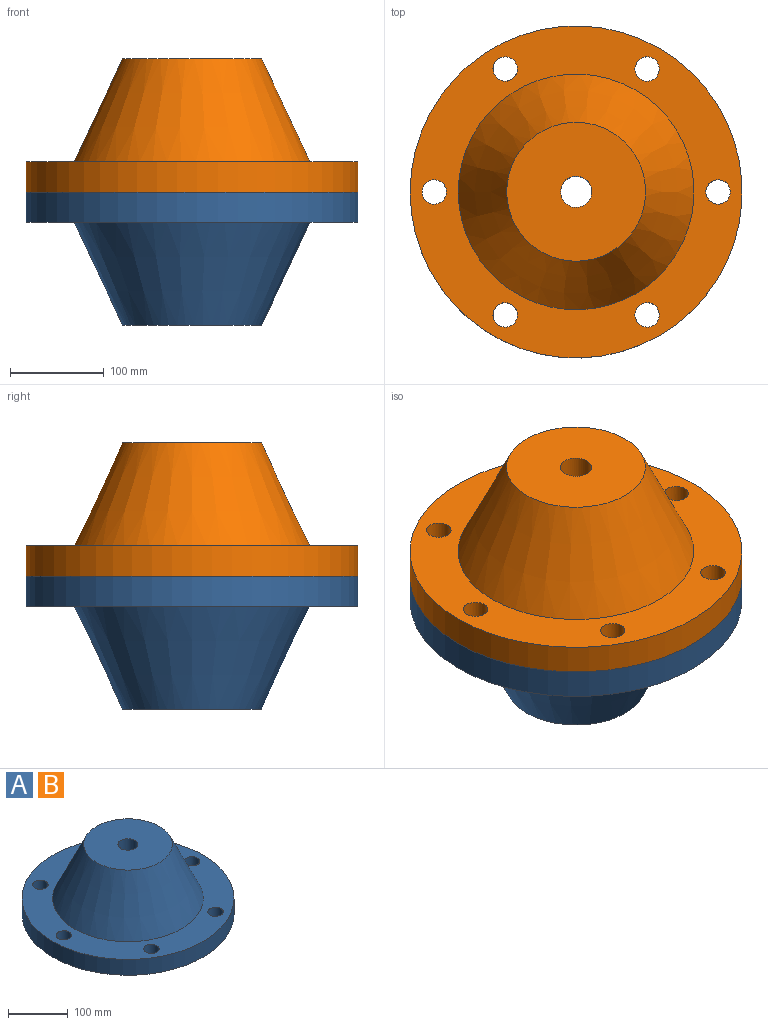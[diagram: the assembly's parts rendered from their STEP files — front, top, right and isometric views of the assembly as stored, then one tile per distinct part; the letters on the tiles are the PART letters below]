
ASSEMBLY  parts=2 mates=1
PART A: 16 faces, bbox 355.1x355.1x142.5 mm
  f0: cylinder r=107.62mm len=215.23mm, axis (0,0,-1), area 19193.4mm2, adj f1,f9
  f1: plane 355.08x355.08mm, normal (0,0,-1), area 59434.8mm2, adj f0,f2,f10,f11,f12,f13,f14,f15
  f2: cylinder r=177.54mm len=355.08mm, axis (0,0,-1), area 35930.7mm2, adj f1,f3
  f3: plane 355.08x355.08mm, normal (0,0,1), area 45903.4mm2, adj f2,f4,f10,f11,f12,f13,f14,f15
  f4: cone r=126.05mm half-angle=25.1deg, axis (0,0,-1), area 76705.1mm2, adj f3,f5
  f5: plane 148.55x148.55mm, normal (0,0,1), area 16456.2mm2, adj f4,f6
  f6: cylinder r=16.7mm len=36.11mm, axis (0,0,-1), area 3789.7mm2, adj f5,f7
  f7: plane 54.72x54.72mm, normal (0,0,-1), area 1475.2mm2, adj f6,f8
  f8: cylinder r=27.36mm len=78.05mm, axis (0,0,-1), area 13416.9mm2, adj f7,f9
  f9: plane 215.23x215.23mm, normal (0,0,-1), area 34031.7mm2, adj f0,f8
  f10: cylinder r=13.05mm len=32.21mm, axis (0,0,1), area 2640.3mm2, adj f1,f3
  f11: cylinder r=13.05mm len=32.21mm, axis (0,0,1), area 2640.3mm2, adj f1,f3
  f12: cylinder r=13.05mm len=32.21mm, axis (0,0,1), area 2640.3mm2, adj f1,f3
  f13: cylinder r=13.05mm len=32.21mm, axis (0,0,1), area 2640.3mm2, adj f1,f3
  f14: cylinder r=13.05mm len=32.21mm, axis (0,0,1), area 2640.3mm2, adj f1,f3
  f15: cylinder r=13.05mm len=32.21mm, axis (0,0,1), area 2640.3mm2, adj f1,f3
PART B: same geometry as A
PLACE A rot(axis=(1,0,0),180deg) t=(0,0,0)mm
PLACE B at identity fixed
MATE fastened B.f0 <-> A.f0  axis (0,0,-1) through (0,0,0)mm
